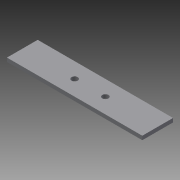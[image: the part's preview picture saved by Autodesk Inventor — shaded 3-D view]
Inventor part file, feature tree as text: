
AUTODESK INVENTOR PART (.ipt)
format: ipt  version: 2013 (Build 170138000, 138)  size: 155,648 bytes
history: native  units: in
note: dims shown in document units (in); Inventor stores cm internally (conversion verified against a paired STEP export)
features: other x5, sketch x4, sheet_metal_op x3
ambient origin geometry x8: Origin, YZ Plane, XZ Plane, XY Plane, X Axis, Y Axis, Z Axis, Center Point
bodies: Solid1 (feature_tree)
feature tree (12):
  sheet_metal_op  "Face1"
  sheet_metal_op  "Face2"
  other  "Plate1"
  sketch  "Sketch5"  dims[d0=1.0in]
  sketch  "Sketch10"  dims[d1=6.0in]
  sketch  "Sketch12"  dims[d2=0.125in]
  sketch  "Sketch13"  dims[d33=0.2in d34=0.2in d35=1.0in d37=0.125in d38=0.0in d55=0.5in d56=0.5in d57=2.2in d58=1.5in d59=1.0in d60=0.266in d61=0.5in d62=0.5in d63=0.266in d64=0.5in d65=0.5in d66=0.125in d67=0.0in d71=0.125in d72=0.0in d73=1.0in d74=1.5in d75=1.0in d76=1.5in d77=1.0in d78=0.266in d79=0.266in d80=0.266in d81=0.5in d82=0.5in d83=0.5in d84=0.5in d85=0.5in d86=0.5in d87=1.5in d88=0.125in d89=0.125in d90=0.0625in d91=0.25in d92=0.125in]
  other  "Plate5"
  sheet_metal_op  "Bend4"
  other  "Cut1"
  other  "Cut6"
  other  "Cut7"
